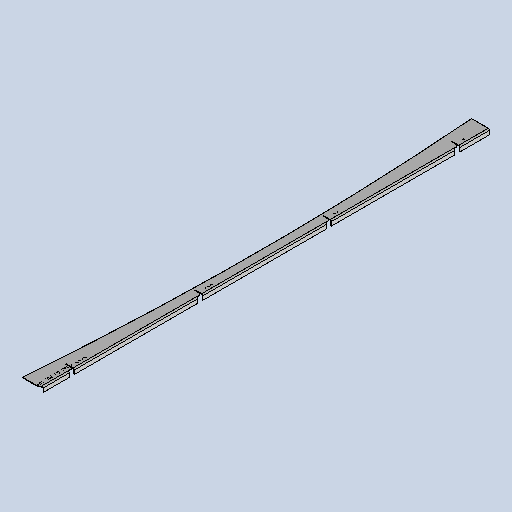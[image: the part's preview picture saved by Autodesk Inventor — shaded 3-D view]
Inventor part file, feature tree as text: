
AUTODESK INVENTOR PART (.ipt)
format: ipt  version: 2025 (Build 290162010, 162A)  size: 457,216 bytes
history: native  units: mm
features: other x6, sheet_metal_op x4, sketch x4, extrude x1, pattern_linear x1, projected_geometry x1
ambient origin geometry x8: Origin, YZ Plane, XZ Plane, XY Plane, X Axis, Y Axis, Z Axis, Center Point
bodies: Body1 (feature_tree)
feature tree (17):
  sheet_metal_op  "Face2"
  sheet_metal_op  "Flange2"
  extrude  "Extrusion2"  Depth=2.0mm
  pattern_linear  "Rectangular Pattern3"  Spacing1=2.75mm  [1 undecoded]
  other  "Mark1"
  other  "Corner Chamfer1"
  other  "A-Side Definition"
  sketch  "Sketch1"  dims[d25=50.0mm d33=50.0mm d46=2.0mm]
  other  "Plate3"
  sketch  "Sketch3"  dims[d47=2.0mm]
  other  "Plate4"
  sheet_metal_op  "Bend2"
  sheet_metal_op  "Corner2"
  sketch  "Sketch5"  dims[d48=1.0mm]
  projected_geometry  "Projected Loop2"
  sketch  "Sketch6"  dims[d49=4.0mm d50=2.75mm d51=20.0mm d52=90.0deg d53=2.75mm d54=8.0mm d55=2.0mm d56=2.75mm d57=500.0mm d58=500.0mm d59=500.0mm d60=500.0mm d61=500.0mm d69=1735.171219mm d70=2.0mm d71=0.0mm d72=0.0mm d76=61.625948mm d79=30.0mm d80=39.195636mm d102=62.276234mm d104=39.411954mm d106=2.0mm d107=20.0mm d108=116.0mm d112=31.0mm d113=40.0mm d115=500.0mm d120=200.0mm d121=12.0mm d123=5.0mm d126=50.0mm d127=25.0mm d135=25.0mm d136=25.0mm d137=25.0mm d141=1745.171mm d142=500.0mm d143=500.0mm d144=500.0mm d145=6.0mm d146=6.0mm d147=45.0deg d148=70.0mm d149=11053.0mm d150=71.959mm d151=23.736478mm d153=10.0mm]
  other  "Definition1"
note: 1 required parameter value undecoded (feature->parameter linkage not recoverable at this tier; creation-order binding heuristic only, values carry confidence <= 0.55)
